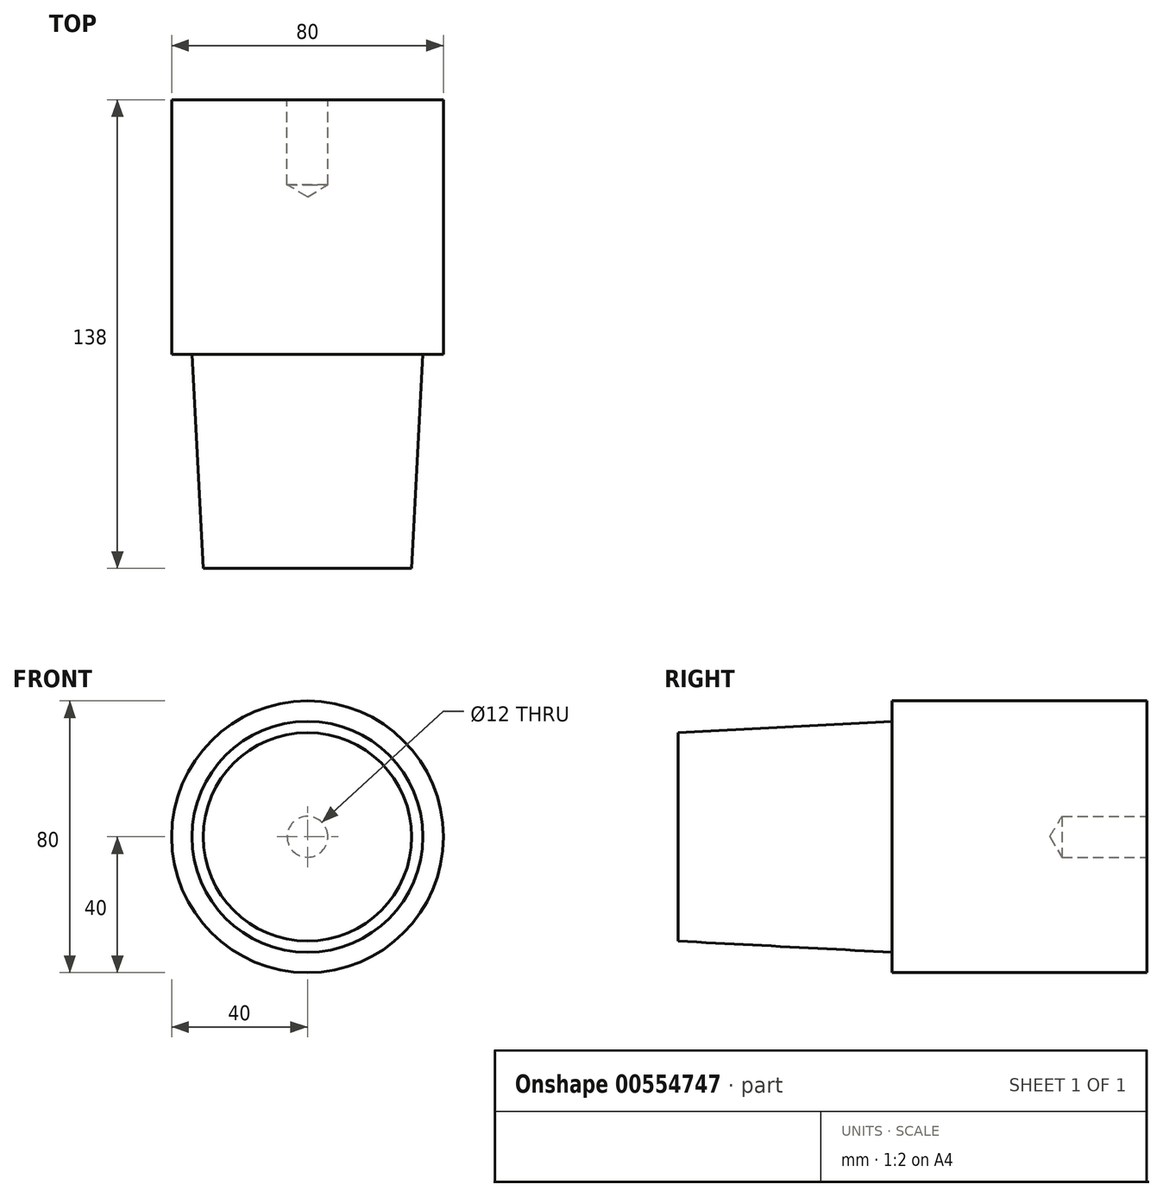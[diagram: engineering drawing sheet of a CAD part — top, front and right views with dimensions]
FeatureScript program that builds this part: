
annotation { "Feature Type Name" : "Feature", "Feature Type Description" : "" }
export const myFeature = defineFeature(function(context is Context, id is Id, definition is map)
    precondition{}
    {
        {
            var Q0;
            Q0=qCreatedBy(makeId("Front.planeOp"),FACE);
            var sketch = newSketch(context, id + "F0", { "sketchPlane" : qUnion([Q0])});
            skCircle(sketch, "E0", {"center": v(0, 0) * mm, "radius": 40 * mm});
            skSolve(sketch);
        }
        {
            var Q0;
            Q0 = qSketchRegion(id + "F0", true);
            extrude(context, id + "F1", {"entities" : qUnion([Q0]), "depth" : 75 * mm, "offsetDistance" : 25 * mm});
        }
        {
            var Q0;
            Q0=makeQuery(id+"F1.opExtrude","CAP_FACE",FACE,{"disambiguationData":[OSD([sQuery(id+"F0.wireOp",EDGE,"E0")])],"isStart":false});
            var sketch = newSketch(context, id + "F2", { "sketchPlane" : qUnion([Q0])});
            skCircle(sketch, "E1", {"center": v(0, 0) * mm, "radius": 34 * mm});
            skSolve(sketch);
        }
        {
            var Q0;
            Q0 = qSketchRegion(id + "F2", true);
            extrude(context, id + "F3", {"entities" : qUnion([Q0]), "operationType" : NewBodyOperationType.ADD, "depth" : 63 * mm, "offsetDistance" : 25 * mm, "hasDraft" : true, "draftAngle" : 3 * degree, "draftPullDirection" : true});
        }
        {
            var Q0;
            Q0=sQuery(id+"F0.wireOp",VERTEX,"E0.center");
            var Q1;
            Q1=makeQuery(id+"F1.opExtrude","SWEPT_BODY",BODY,{"disambiguationData":[OSD([sQuery(id+"F0.wireOp",EDGE,"E0")])]});
            hole(context, id + "F4", {"style" : HoleStyle.SIMPLE, "endStyle" : HoleEndStyle.BLIND, "oppositeDirection" : true, "holeDiameter" : 12 * mm, "holeDepth" : 25 * mm, "isTappedThrough" : true, "tappedDepth" : 12 * mm, "tapClearance" : 3, "startFromSketch" : true, "locations" : qUnion([Q0]), "scope" : qUnion([Q1])});
        }
    });
